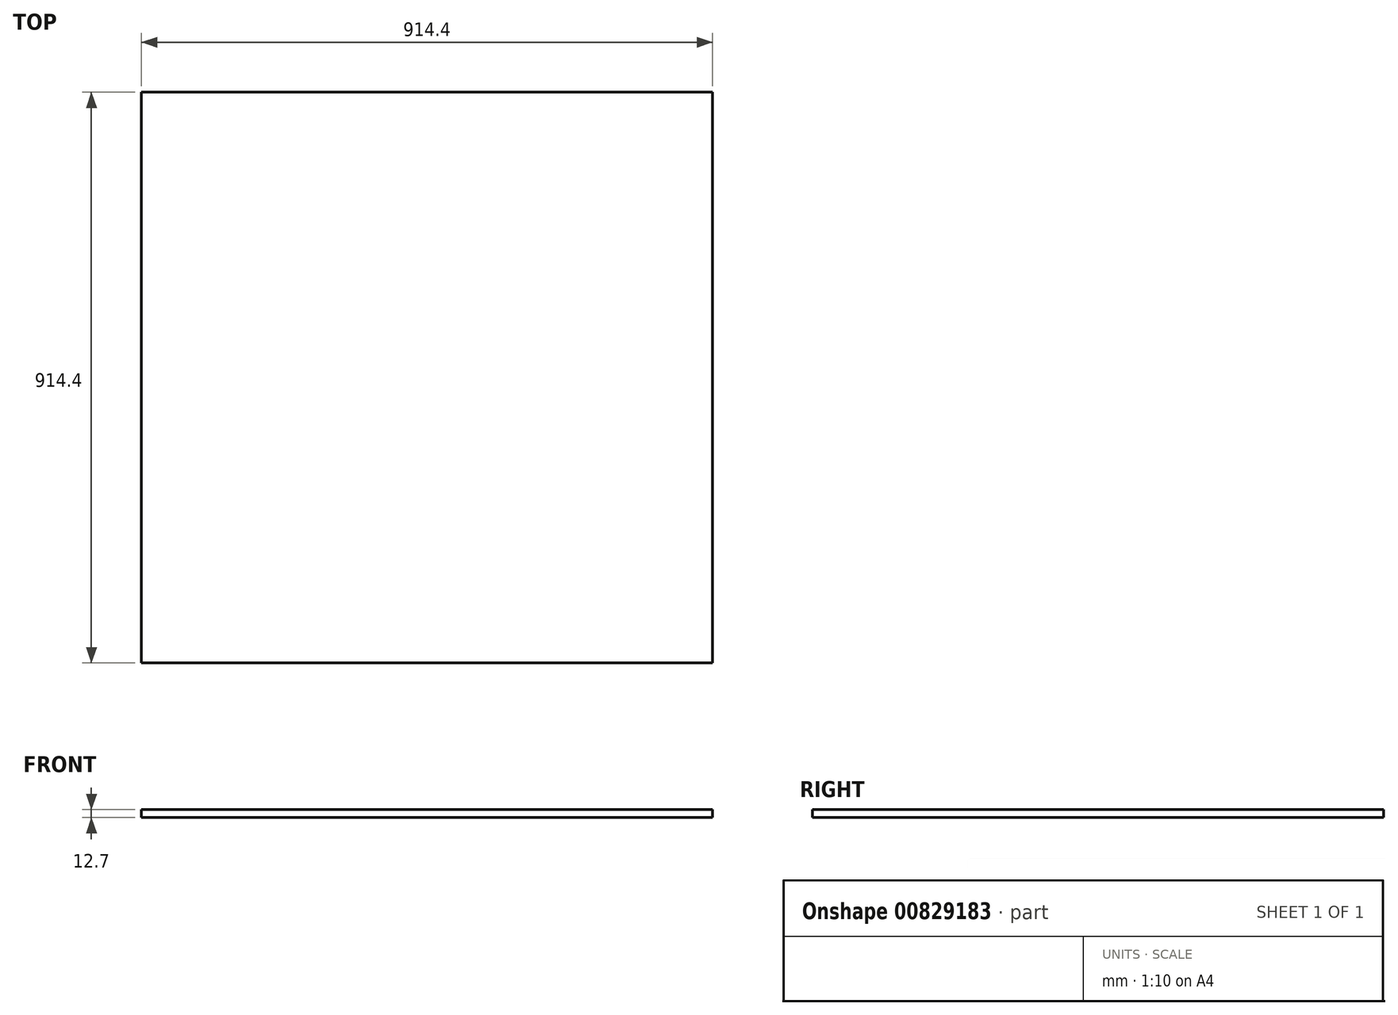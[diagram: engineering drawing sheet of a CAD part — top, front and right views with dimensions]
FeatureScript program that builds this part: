
annotation { "Feature Type Name" : "Feature", "Feature Type Description" : "" }
export const myFeature = defineFeature(function(context is Context, id is Id, definition is map)
    precondition{}
    {
        {
            var Q0;
            Q0=qCreatedBy(makeId("Top.planeOp"),FACE);
            var sketch = newSketch(context, id + "F0", { "sketchPlane" : qUnion([Q0])});
            skLineSegment(sketch, "E0.bottom", {"start": v(457.2, 457.2) * mm, "end": v(-457.2, 457.2) * mm});
            skLineSegment(sketch, "E0.top", {"start": v(457.2, -457.2) * mm, "end": v(-457.2, -457.2) * mm});
            skLineSegment(sketch, "E0.left", {"start": v(457.2, 457.2) * mm, "end": v(457.2, -457.2) * mm});
            skLineSegment(sketch, "E0.right", {"start": v(-457.2, 457.2) * mm, "end": v(-457.2, -457.2) * mm});
            skPoint(sketch, "E0.middle", {"position": v(0, 0) * mm});
            skSolve(sketch);
        }
        {
            var Q0;
            Q0 = qSketchRegion(id + "F0", true);
            extrude(context, id + "F1", {"entities" : qUnion([Q0]), "depth" : 12.7 * mm, "offsetDistance" : 25.4 * mm});
        }
    });
